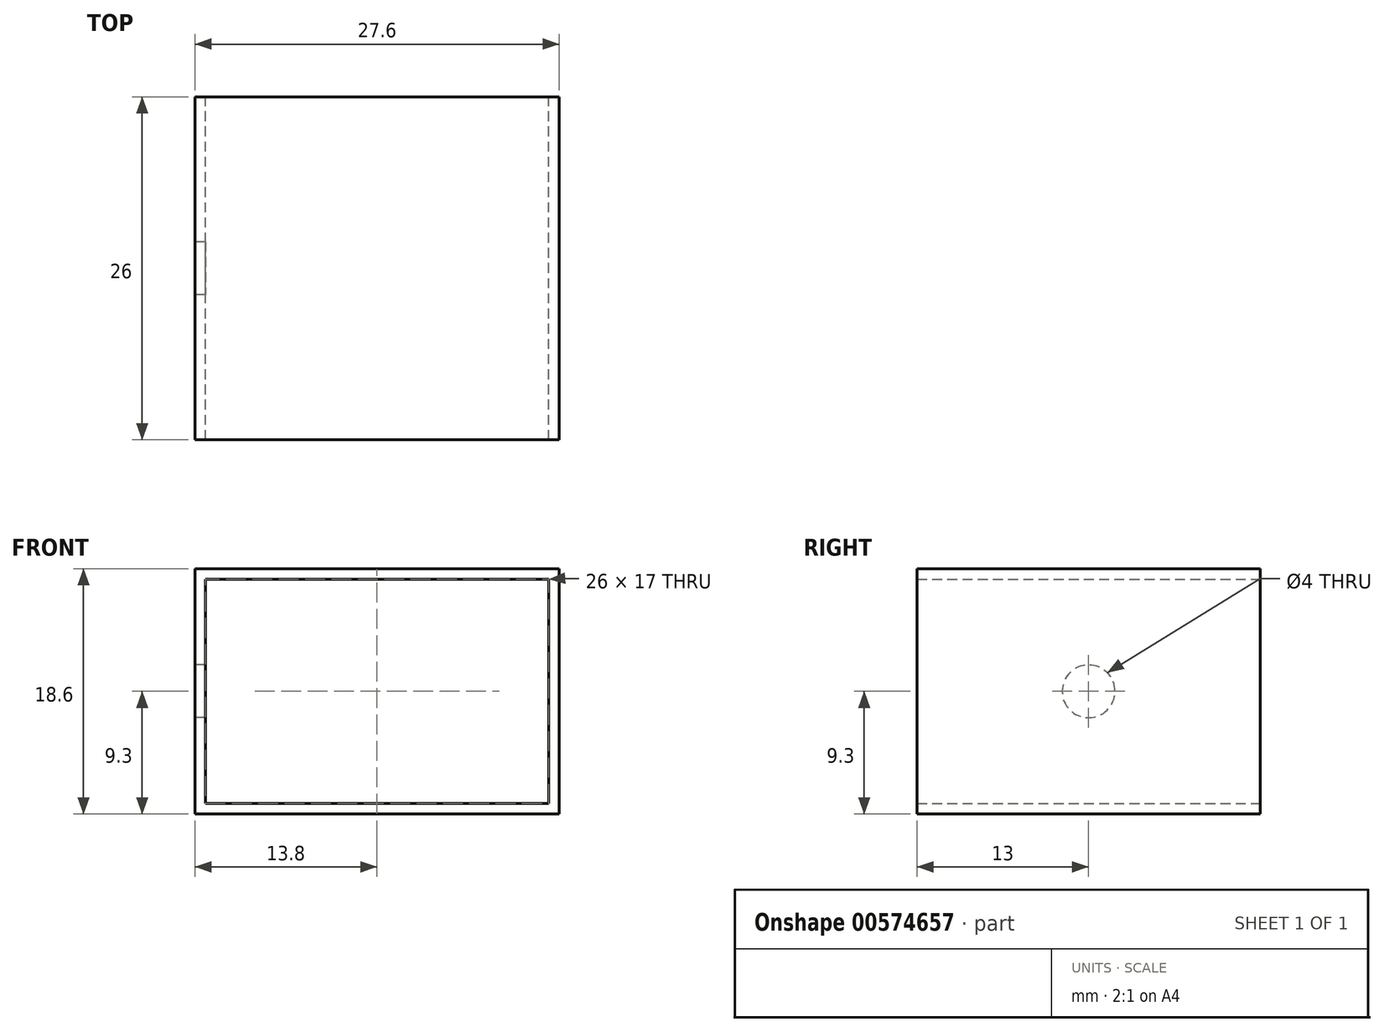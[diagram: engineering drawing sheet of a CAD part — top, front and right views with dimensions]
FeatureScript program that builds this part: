
annotation { "Feature Type Name" : "Feature", "Feature Type Description" : "" }
export const myFeature = defineFeature(function(context is Context, id is Id, definition is map)
    precondition{}
    {
        {
            var Q0;
            Q0=qCreatedBy(makeId("Front.planeOp"),FACE);
            var sketch = newSketch(context, id + "F0", { "sketchPlane" : qUnion([Q0])});
            skLineSegment(sketch, "E0.bottom", {"start": v(13, -8.5) * mm, "end": v(-13, -8.5) * mm});
            skLineSegment(sketch, "E0.top", {"start": v(13, 8.5) * mm, "end": v(-13, 8.5) * mm});
            skLineSegment(sketch, "E0.left", {"start": v(13, -8.5) * mm, "end": v(13, 8.5) * mm});
            skLineSegment(sketch, "E0.right", {"start": v(-13, -8.5) * mm, "end": v(-13, 8.5) * mm});
            skPoint(sketch, "E0.middle", {"position": v(0, 0) * mm});
            skLineSegment(sketch, "E1.bottom", {"start": v(13.8, -9.3) * mm, "end": v(-13.8, -9.3) * mm});
            skLineSegment(sketch, "E1.top", {"start": v(13.8, 9.3) * mm, "end": v(-13.8, 9.3) * mm});
            skLineSegment(sketch, "E1.left", {"start": v(13.8, -9.3) * mm, "end": v(13.8, 9.3) * mm});
            skLineSegment(sketch, "E1.right", {"start": v(-13.8, -9.3) * mm, "end": v(-13.8, 9.3) * mm});
            skSolve(sketch);
        }
        {
            var Q0;
            Q0 = qSketchRegion(id + "F0", true);
            extrude(context, id + "F1", {"entities" : qUnion([Q0]), "depth" : 26 * mm, "offsetDistance" : 25 * mm});
        }
        {
            var Q0;
            Q0=makeQuery(id+"F1.opExtrude","SWEPT_FACE",FACE,{"disambiguationData":[OSD([sQuery(id+"F0.wireOp",EDGE,"E1.right")])]});
            var sketch = newSketch(context, id + "F2", { "sketchPlane" : qUnion([Q0])});
            skCircle(sketch, "E2", {"center": v(13, 0) * mm, "radius": 2 * mm});
            skSolve(sketch);
        }
        {
            var Q0;
            Q0 = qSketchRegion(id + "F2", true);
            extrude(context, id + "F3", {"entities" : qUnion([Q0]), "operationType" : NewBodyOperationType.REMOVE, "oppositeDirection" : true, "depth" : 3 * mm, "offsetDistance" : 25 * mm});
        }
    });
